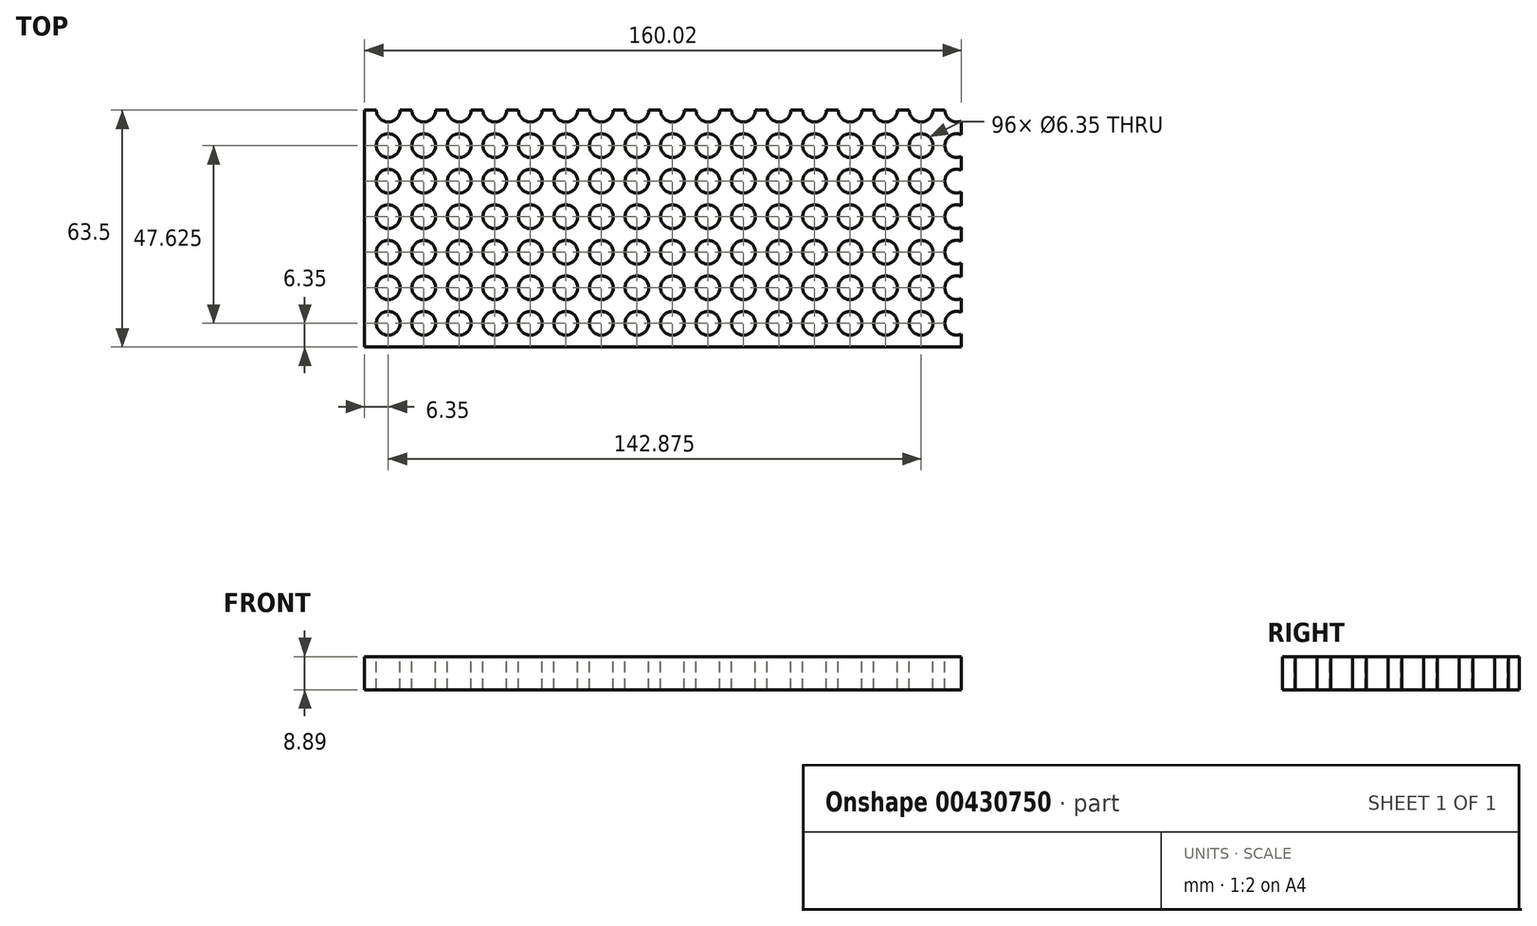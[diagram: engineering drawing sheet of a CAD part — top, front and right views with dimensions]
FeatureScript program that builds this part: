
annotation { "Feature Type Name" : "Feature", "Feature Type Description" : "" }
export const myFeature = defineFeature(function(context is Context, id is Id, definition is map)
    precondition{}
    {
        {
            var Q0;
            Q0=qCreatedBy(makeId("Top.planeOp"),FACE);
            var sketch = newSketch(context, id + "F0", { "sketchPlane" : qUnion([Q0])});
            skLineSegment(sketch, "E0", {"start": v(0, 0) * mm, "end": v(0, 63.5) * mm});
            skLineSegment(sketch, "E1", {"start": v(0, 63.5) * mm, "end": v(160.02, 63.5) * mm});
            skLineSegment(sketch, "E2", {"start": v(160.02, 63.5) * mm, "end": v(160.02, 0) * mm});
            skLineSegment(sketch, "E3", {"start": v(160.02, 0) * mm, "end": v(0, 0) * mm});
            skSolve(sketch);
        }
        {
            var Q0;
            Q0=makeQuery(id+"F0.imprint","IMPRINT",FACE,{"disambiguationData":[TD([[makeQuery(id+"F0.imprint","IMPRINT",EDGE,{"derivedFrom":sQuery(id+"F0.wireOp",EDGE,"E0")}),-1.0]])]});
            extrude(context, id + "F1", {"entities" : qUnion([Q0]), "depth" : 8.9 * mm, "offsetDistance" : 25.4 * mm});
        }
        {
            var Q0;
            Q0=makeQuery(id+"F1.opExtrude","CAP_FACE",FACE,{"disambiguationData":[OSD([sQuery(id+"F0.wireOp",EDGE,"E0"),sQuery(id+"F0.wireOp",EDGE,"E1"),sQuery(id+"F0.wireOp",EDGE,"E2"),sQuery(id+"F0.wireOp",EDGE,"E3")])],"isStart":false});
            var sketch = newSketch(context, id + "F2", { "sketchPlane" : qUnion([Q0])});
            skLineSegment(sketch, "E4", {"start": v(0, 0) * mm, "end": v(0, 6.35) * mm});
            skLineSegment(sketch, "E5", {"start": v(0, 6.35) * mm, "end": v(6.35, 6.35) * mm});
            skCircle(sketch, "E6", {"center": v(6.35, 6.35) * mm, "radius": 3.18 * mm});
            skCircle(sketch, "E7.0.1.0", {"center": v(6.35, 15.88) * mm, "radius": 3.18 * mm});
            skCircle(sketch, "E7.0.2.0", {"center": v(6.35, 25.4) * mm, "radius": 3.18 * mm});
            skCircle(sketch, "E7.0.3.0", {"center": v(6.35, 34.92) * mm, "radius": 3.18 * mm});
            skCircle(sketch, "E7.0.4.0", {"center": v(6.35, 44.45) * mm, "radius": 3.18 * mm});
            skCircle(sketch, "E7.0.5.0", {"center": v(6.35, 53.97) * mm, "radius": 3.18 * mm});
            skCircle(sketch, "E7.0.6.0", {"center": v(6.35, 63.5) * mm, "radius": 3.18 * mm});
            skCircle(sketch, "E7.1.0.0", {"center": v(15.88, 6.35) * mm, "radius": 3.18 * mm});
            skCircle(sketch, "E7.1.1.0", {"center": v(15.88, 15.88) * mm, "radius": 3.18 * mm});
            skCircle(sketch, "E7.1.2.0", {"center": v(15.88, 25.4) * mm, "radius": 3.18 * mm});
            skCircle(sketch, "E7.1.3.0", {"center": v(15.88, 34.92) * mm, "radius": 3.18 * mm});
            skCircle(sketch, "E7.1.4.0", {"center": v(15.88, 44.45) * mm, "radius": 3.18 * mm});
            skCircle(sketch, "E7.1.5.0", {"center": v(15.88, 53.97) * mm, "radius": 3.18 * mm});
            skCircle(sketch, "E7.1.6.0", {"center": v(15.88, 63.5) * mm, "radius": 3.18 * mm});
            skCircle(sketch, "E7.2.0.0", {"center": v(25.4, 6.35) * mm, "radius": 3.18 * mm});
            skCircle(sketch, "E7.2.1.0", {"center": v(25.4, 15.88) * mm, "radius": 3.18 * mm});
            skCircle(sketch, "E7.2.2.0", {"center": v(25.4, 25.4) * mm, "radius": 3.18 * mm});
            skCircle(sketch, "E7.2.3.0", {"center": v(25.4, 34.92) * mm, "radius": 3.18 * mm});
            skCircle(sketch, "E7.2.4.0", {"center": v(25.4, 44.45) * mm, "radius": 3.18 * mm});
            skCircle(sketch, "E7.2.5.0", {"center": v(25.4, 53.97) * mm, "radius": 3.18 * mm});
            skCircle(sketch, "E7.2.6.0", {"center": v(25.4, 63.5) * mm, "radius": 3.18 * mm});
            skCircle(sketch, "E7.3.0.0", {"center": v(34.92, 6.35) * mm, "radius": 3.18 * mm});
            skCircle(sketch, "E7.3.1.0", {"center": v(34.92, 15.88) * mm, "radius": 3.18 * mm});
            skCircle(sketch, "E7.3.2.0", {"center": v(34.92, 25.4) * mm, "radius": 3.18 * mm});
            skCircle(sketch, "E7.3.3.0", {"center": v(34.92, 34.92) * mm, "radius": 3.18 * mm});
            skCircle(sketch, "E7.3.4.0", {"center": v(34.92, 44.45) * mm, "radius": 3.18 * mm});
            skCircle(sketch, "E7.3.5.0", {"center": v(34.92, 53.97) * mm, "radius": 3.18 * mm});
            skCircle(sketch, "E7.3.6.0", {"center": v(34.92, 63.5) * mm, "radius": 3.18 * mm});
            skCircle(sketch, "E7.4.0.0", {"center": v(44.45, 6.35) * mm, "radius": 3.18 * mm});
            skCircle(sketch, "E7.4.1.0", {"center": v(44.45, 15.88) * mm, "radius": 3.18 * mm});
            skCircle(sketch, "E7.4.2.0", {"center": v(44.45, 25.4) * mm, "radius": 3.18 * mm});
            skCircle(sketch, "E7.4.3.0", {"center": v(44.45, 34.92) * mm, "radius": 3.18 * mm});
            skCircle(sketch, "E7.4.4.0", {"center": v(44.45, 44.45) * mm, "radius": 3.18 * mm});
            skCircle(sketch, "E7.4.5.0", {"center": v(44.45, 53.97) * mm, "radius": 3.18 * mm});
            skCircle(sketch, "E7.4.6.0", {"center": v(44.45, 63.5) * mm, "radius": 3.18 * mm});
            skCircle(sketch, "E7.5.0.0", {"center": v(53.97, 6.35) * mm, "radius": 3.18 * mm});
            skCircle(sketch, "E7.5.1.0", {"center": v(53.97, 15.88) * mm, "radius": 3.18 * mm});
            skCircle(sketch, "E7.5.2.0", {"center": v(53.97, 25.4) * mm, "radius": 3.18 * mm});
            skCircle(sketch, "E7.5.3.0", {"center": v(53.97, 34.92) * mm, "radius": 3.18 * mm});
            skCircle(sketch, "E7.5.4.0", {"center": v(53.97, 44.45) * mm, "radius": 3.18 * mm});
            skCircle(sketch, "E7.5.5.0", {"center": v(53.97, 53.97) * mm, "radius": 3.18 * mm});
            skCircle(sketch, "E7.5.6.0", {"center": v(53.97, 63.5) * mm, "radius": 3.18 * mm});
            skCircle(sketch, "E7.6.0.0", {"center": v(63.5, 6.35) * mm, "radius": 3.18 * mm});
            skCircle(sketch, "E7.6.1.0", {"center": v(63.5, 15.88) * mm, "radius": 3.18 * mm});
            skCircle(sketch, "E7.6.2.0", {"center": v(63.5, 25.4) * mm, "radius": 3.18 * mm});
            skCircle(sketch, "E7.6.3.0", {"center": v(63.5, 34.92) * mm, "radius": 3.18 * mm});
            skCircle(sketch, "E7.6.4.0", {"center": v(63.5, 44.45) * mm, "radius": 3.18 * mm});
            skCircle(sketch, "E7.6.5.0", {"center": v(63.5, 53.97) * mm, "radius": 3.18 * mm});
            skCircle(sketch, "E7.6.6.0", {"center": v(63.5, 63.5) * mm, "radius": 3.18 * mm});
            skCircle(sketch, "E7.7.0.0", {"center": v(73.02, 6.35) * mm, "radius": 3.18 * mm});
            skCircle(sketch, "E7.7.1.0", {"center": v(73.02, 15.88) * mm, "radius": 3.18 * mm});
            skCircle(sketch, "E7.7.2.0", {"center": v(73.02, 25.4) * mm, "radius": 3.18 * mm});
            skCircle(sketch, "E7.7.3.0", {"center": v(73.02, 34.92) * mm, "radius": 3.18 * mm});
            skCircle(sketch, "E7.7.4.0", {"center": v(73.02, 44.45) * mm, "radius": 3.18 * mm});
            skCircle(sketch, "E7.7.5.0", {"center": v(73.02, 53.97) * mm, "radius": 3.18 * mm});
            skCircle(sketch, "E7.7.6.0", {"center": v(73.02, 63.5) * mm, "radius": 3.18 * mm});
            skCircle(sketch, "E7.8.0.0", {"center": v(82.55, 6.35) * mm, "radius": 3.18 * mm});
            skCircle(sketch, "E7.8.1.0", {"center": v(82.55, 15.88) * mm, "radius": 3.18 * mm});
            skCircle(sketch, "E7.8.2.0", {"center": v(82.55, 25.4) * mm, "radius": 3.18 * mm});
            skCircle(sketch, "E7.8.3.0", {"center": v(82.55, 34.92) * mm, "radius": 3.18 * mm});
            skCircle(sketch, "E7.8.4.0", {"center": v(82.55, 44.45) * mm, "radius": 3.18 * mm});
            skCircle(sketch, "E7.8.5.0", {"center": v(82.55, 53.97) * mm, "radius": 3.18 * mm});
            skCircle(sketch, "E7.8.6.0", {"center": v(82.55, 63.5) * mm, "radius": 3.18 * mm});
            skCircle(sketch, "E7.9.0.0", {"center": v(92.07, 6.35) * mm, "radius": 3.18 * mm});
            skCircle(sketch, "E7.9.1.0", {"center": v(92.07, 15.88) * mm, "radius": 3.18 * mm});
            skCircle(sketch, "E7.9.2.0", {"center": v(92.07, 25.4) * mm, "radius": 3.18 * mm});
            skCircle(sketch, "E7.9.3.0", {"center": v(92.07, 34.92) * mm, "radius": 3.18 * mm});
            skCircle(sketch, "E7.9.4.0", {"center": v(92.07, 44.45) * mm, "radius": 3.18 * mm});
            skCircle(sketch, "E7.9.5.0", {"center": v(92.07, 53.97) * mm, "radius": 3.18 * mm});
            skCircle(sketch, "E7.9.6.0", {"center": v(92.07, 63.5) * mm, "radius": 3.18 * mm});
            skCircle(sketch, "E7.10.0.0", {"center": v(101.6, 6.35) * mm, "radius": 3.18 * mm});
            skCircle(sketch, "E7.10.1.0", {"center": v(101.6, 15.88) * mm, "radius": 3.18 * mm});
            skCircle(sketch, "E7.10.2.0", {"center": v(101.6, 25.4) * mm, "radius": 3.18 * mm});
            skCircle(sketch, "E7.10.3.0", {"center": v(101.6, 34.92) * mm, "radius": 3.18 * mm});
            skCircle(sketch, "E7.10.4.0", {"center": v(101.6, 44.45) * mm, "radius": 3.18 * mm});
            skCircle(sketch, "E7.10.5.0", {"center": v(101.6, 53.97) * mm, "radius": 3.18 * mm});
            skCircle(sketch, "E7.10.6.0", {"center": v(101.6, 63.5) * mm, "radius": 3.18 * mm});
            skCircle(sketch, "E7.11.0.0", {"center": v(111.12, 6.35) * mm, "radius": 3.18 * mm});
            skCircle(sketch, "E7.11.1.0", {"center": v(111.12, 15.88) * mm, "radius": 3.18 * mm});
            skCircle(sketch, "E7.11.2.0", {"center": v(111.12, 25.4) * mm, "radius": 3.18 * mm});
            skCircle(sketch, "E7.11.3.0", {"center": v(111.12, 34.92) * mm, "radius": 3.18 * mm});
            skCircle(sketch, "E7.11.4.0", {"center": v(111.12, 44.45) * mm, "radius": 3.18 * mm});
            skCircle(sketch, "E7.11.5.0", {"center": v(111.12, 53.97) * mm, "radius": 3.18 * mm});
            skCircle(sketch, "E7.11.6.0", {"center": v(111.12, 63.5) * mm, "radius": 3.18 * mm});
            skCircle(sketch, "E7.12.0.0", {"center": v(120.65, 6.35) * mm, "radius": 3.18 * mm});
            skCircle(sketch, "E7.12.1.0", {"center": v(120.65, 15.88) * mm, "radius": 3.18 * mm});
            skCircle(sketch, "E7.12.2.0", {"center": v(120.65, 25.4) * mm, "radius": 3.18 * mm});
            skCircle(sketch, "E7.12.3.0", {"center": v(120.65, 34.92) * mm, "radius": 3.18 * mm});
            skCircle(sketch, "E7.12.4.0", {"center": v(120.65, 44.45) * mm, "radius": 3.18 * mm});
            skCircle(sketch, "E7.12.5.0", {"center": v(120.65, 53.97) * mm, "radius": 3.18 * mm});
            skCircle(sketch, "E7.12.6.0", {"center": v(120.65, 63.5) * mm, "radius": 3.18 * mm});
            skCircle(sketch, "E7.13.0.0", {"center": v(130.17, 6.35) * mm, "radius": 3.18 * mm});
            skCircle(sketch, "E7.13.1.0", {"center": v(130.17, 15.88) * mm, "radius": 3.18 * mm});
            skCircle(sketch, "E7.13.2.0", {"center": v(130.17, 25.4) * mm, "radius": 3.18 * mm});
            skCircle(sketch, "E7.13.3.0", {"center": v(130.17, 34.92) * mm, "radius": 3.18 * mm});
            skCircle(sketch, "E7.13.4.0", {"center": v(130.17, 44.45) * mm, "radius": 3.18 * mm});
            skCircle(sketch, "E7.13.5.0", {"center": v(130.17, 53.97) * mm, "radius": 3.18 * mm});
            skCircle(sketch, "E7.13.6.0", {"center": v(130.17, 63.5) * mm, "radius": 3.18 * mm});
            skCircle(sketch, "E7.14.0.0", {"center": v(139.7, 6.35) * mm, "radius": 3.18 * mm});
            skCircle(sketch, "E7.14.1.0", {"center": v(139.7, 15.88) * mm, "radius": 3.18 * mm});
            skCircle(sketch, "E7.14.2.0", {"center": v(139.7, 25.4) * mm, "radius": 3.18 * mm});
            skCircle(sketch, "E7.14.3.0", {"center": v(139.7, 34.92) * mm, "radius": 3.18 * mm});
            skCircle(sketch, "E7.14.4.0", {"center": v(139.7, 44.45) * mm, "radius": 3.18 * mm});
            skCircle(sketch, "E7.14.5.0", {"center": v(139.7, 53.97) * mm, "radius": 3.18 * mm});
            skCircle(sketch, "E7.14.6.0", {"center": v(139.7, 63.5) * mm, "radius": 3.18 * mm});
            skLineSegment(sketch, "E7.direction1", {"start": v(6.35, 6.35) * mm, "end": v(15.88, 6.35) * mm, "construction": true});
            skLineSegment(sketch, "E7.direction2", {"start": v(6.35, 6.35) * mm, "end": v(6.35, 15.88) * mm, "construction": true});
            skCircle(sketch, "E8.0.15.0", {"center": v(149.22, 6.35) * mm, "radius": 3.18 * mm});
            skCircle(sketch, "E8.0.15.1", {"center": v(149.22, 15.88) * mm, "radius": 3.18 * mm});
            skCircle(sketch, "E8.0.15.2", {"center": v(149.22, 25.4) * mm, "radius": 3.18 * mm});
            skCircle(sketch, "E8.0.15.3", {"center": v(149.22, 34.92) * mm, "radius": 3.18 * mm});
            skCircle(sketch, "E8.0.15.4", {"center": v(149.22, 44.45) * mm, "radius": 3.18 * mm});
            skCircle(sketch, "E8.0.15.5", {"center": v(149.22, 53.97) * mm, "radius": 3.18 * mm});
            skCircle(sketch, "E8.0.15.6", {"center": v(149.22, 63.5) * mm, "radius": 3.18 * mm});
            skCircle(sketch, "E8.0.16.0", {"center": v(158.75, 6.35) * mm, "radius": 3.18 * mm});
            skCircle(sketch, "E8.0.16.1", {"center": v(158.75, 15.88) * mm, "radius": 3.18 * mm});
            skCircle(sketch, "E8.0.16.2", {"center": v(158.75, 25.4) * mm, "radius": 3.18 * mm});
            skCircle(sketch, "E8.0.16.3", {"center": v(158.75, 34.92) * mm, "radius": 3.18 * mm});
            skCircle(sketch, "E8.0.16.4", {"center": v(158.75, 44.45) * mm, "radius": 3.18 * mm});
            skCircle(sketch, "E8.0.16.5", {"center": v(158.75, 53.97) * mm, "radius": 3.18 * mm});
            skCircle(sketch, "E8.0.16.6", {"center": v(158.75, 63.5) * mm, "radius": 3.18 * mm});
            skCircle(sketch, "E9.0.0.7", {"center": v(6.35, 73.02) * mm, "radius": 3.18 * mm});
            skCircle(sketch, "E9.0.0.8", {"center": v(6.35, 82.55) * mm, "radius": 3.18 * mm});
            skCircle(sketch, "E9.0.1.7", {"center": v(15.88, 73.02) * mm, "radius": 3.18 * mm});
            skCircle(sketch, "E9.0.1.8", {"center": v(15.88, 82.55) * mm, "radius": 3.18 * mm});
            skCircle(sketch, "E9.0.2.7", {"center": v(25.4, 73.02) * mm, "radius": 3.18 * mm});
            skCircle(sketch, "E9.0.2.8", {"center": v(25.4, 82.55) * mm, "radius": 3.18 * mm});
            skCircle(sketch, "E9.0.3.7", {"center": v(34.92, 73.02) * mm, "radius": 3.18 * mm});
            skCircle(sketch, "E9.0.3.8", {"center": v(34.92, 82.55) * mm, "radius": 3.18 * mm});
            skCircle(sketch, "E9.0.4.7", {"center": v(44.45, 73.02) * mm, "radius": 3.18 * mm});
            skCircle(sketch, "E9.0.4.8", {"center": v(44.45, 82.55) * mm, "radius": 3.18 * mm});
            skCircle(sketch, "E9.0.5.7", {"center": v(53.97, 73.02) * mm, "radius": 3.18 * mm});
            skCircle(sketch, "E9.0.5.8", {"center": v(53.97, 82.55) * mm, "radius": 3.18 * mm});
            skCircle(sketch, "E9.0.6.7", {"center": v(63.5, 73.02) * mm, "radius": 3.18 * mm});
            skCircle(sketch, "E9.0.6.8", {"center": v(63.5, 82.55) * mm, "radius": 3.18 * mm});
            skCircle(sketch, "E9.0.7.7", {"center": v(73.02, 73.02) * mm, "radius": 3.18 * mm});
            skCircle(sketch, "E9.0.7.8", {"center": v(73.02, 82.55) * mm, "radius": 3.18 * mm});
            skCircle(sketch, "E9.0.8.7", {"center": v(82.55, 73.02) * mm, "radius": 3.18 * mm});
            skCircle(sketch, "E9.0.8.8", {"center": v(82.55, 82.55) * mm, "radius": 3.18 * mm});
            skCircle(sketch, "E9.0.9.7", {"center": v(92.07, 73.02) * mm, "radius": 3.18 * mm});
            skCircle(sketch, "E9.0.9.8", {"center": v(92.07, 82.55) * mm, "radius": 3.18 * mm});
            skCircle(sketch, "E9.0.10.7", {"center": v(101.6, 73.02) * mm, "radius": 3.18 * mm});
            skCircle(sketch, "E9.0.10.8", {"center": v(101.6, 82.55) * mm, "radius": 3.18 * mm});
            skCircle(sketch, "E9.0.11.7", {"center": v(111.12, 73.02) * mm, "radius": 3.18 * mm});
            skCircle(sketch, "E9.0.11.8", {"center": v(111.12, 82.55) * mm, "radius": 3.18 * mm});
            skCircle(sketch, "E9.0.12.7", {"center": v(120.65, 73.02) * mm, "radius": 3.18 * mm});
            skCircle(sketch, "E9.0.12.8", {"center": v(120.65, 82.55) * mm, "radius": 3.18 * mm});
            skCircle(sketch, "E9.0.13.7", {"center": v(130.17, 73.02) * mm, "radius": 3.18 * mm});
            skCircle(sketch, "E9.0.13.8", {"center": v(130.17, 82.55) * mm, "radius": 3.18 * mm});
            skCircle(sketch, "E9.0.14.7", {"center": v(139.7, 73.02) * mm, "radius": 3.18 * mm});
            skCircle(sketch, "E9.0.14.8", {"center": v(139.7, 82.55) * mm, "radius": 3.18 * mm});
            skCircle(sketch, "E9.0.15.7", {"center": v(149.22, 73.02) * mm, "radius": 3.18 * mm});
            skCircle(sketch, "E9.0.15.8", {"center": v(149.22, 82.55) * mm, "radius": 3.18 * mm});
            skCircle(sketch, "E9.0.16.7", {"center": v(158.75, 73.02) * mm, "radius": 3.18 * mm});
            skCircle(sketch, "E9.0.16.8", {"center": v(158.75, 82.55) * mm, "radius": 3.18 * mm});
            skSolve(sketch);
        }
        {
            var Q0;
            Q0 = qSketchRegion(id + "F2", true);
            extrude(context, id + "F3", {"entities" : qUnion([Q0]), "operationType" : NewBodyOperationType.REMOVE, "oppositeDirection" : true, "depth" : 25.4 * mm, "offsetDistance" : 25.4 * mm});
        }
    });
